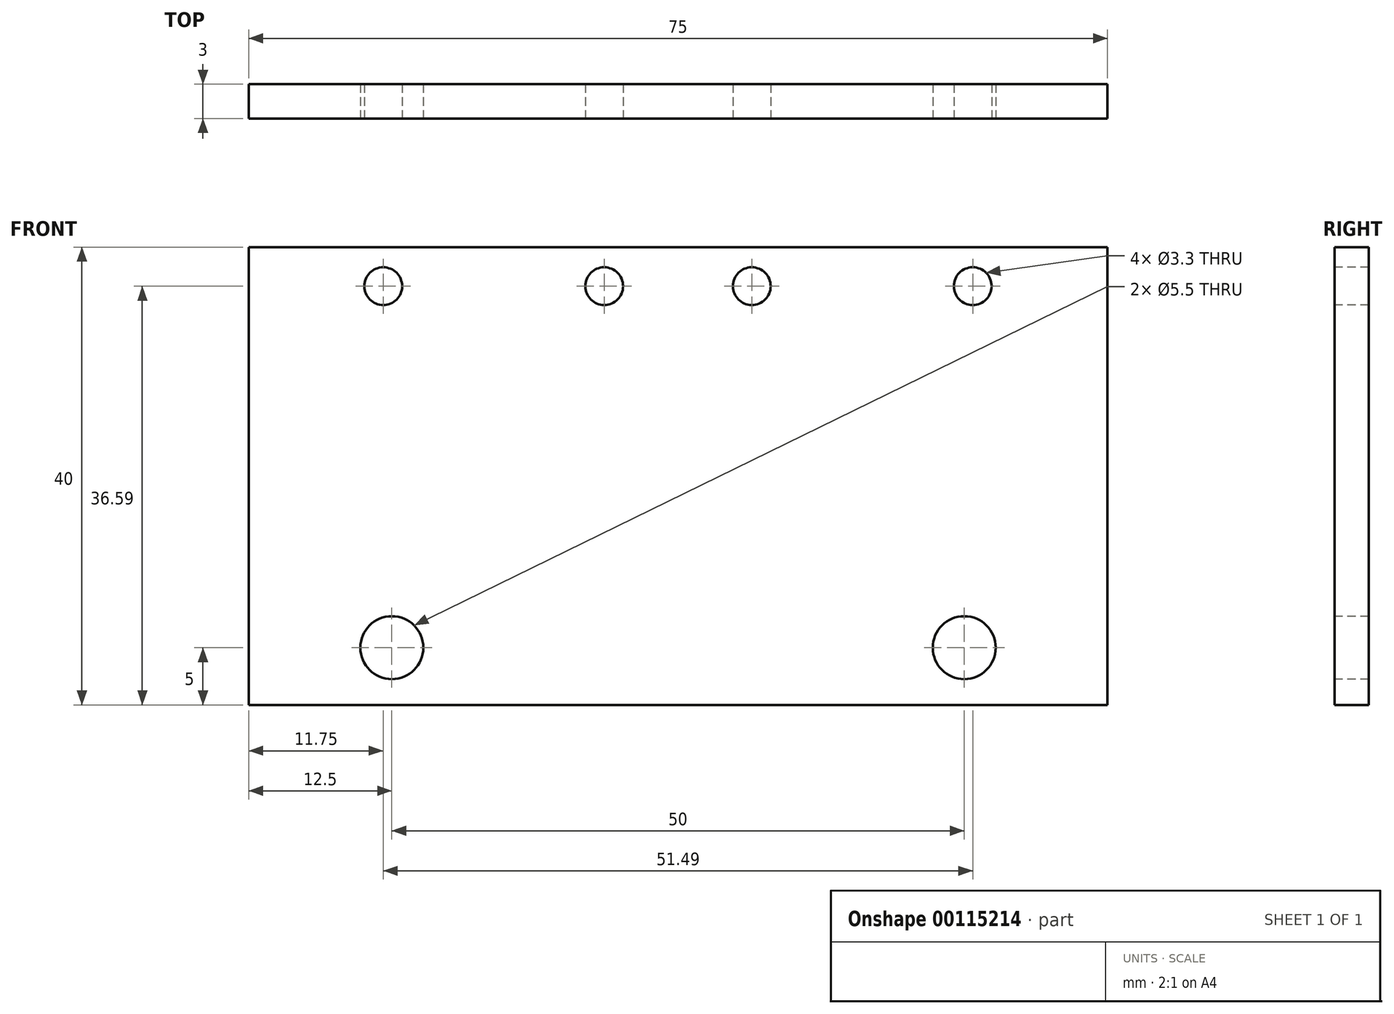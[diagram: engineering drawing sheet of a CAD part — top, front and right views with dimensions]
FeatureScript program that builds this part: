
annotation { "Feature Type Name" : "Feature", "Feature Type Description" : "" }
export const myFeature = defineFeature(function(context is Context, id is Id, definition is map)
    precondition{}
    {
        {
            var Q0;
            Q0=qCreatedBy(makeId("Front.planeOp"),FACE);
            var sketch = newSketch(context, id + "F0", { "sketchPlane" : qUnion([Q0])});
            skLineSegment(sketch, "E0.bottom", {"start": v(0, 0) * mm, "end": v(75, 0) * mm});
            skLineSegment(sketch, "E0.top", {"start": v(0, 40) * mm, "end": v(75, 40) * mm});
            skLineSegment(sketch, "E0.left", {"start": v(0, 0) * mm, "end": v(0, 40) * mm});
            skLineSegment(sketch, "E0.right", {"start": v(75, 0) * mm, "end": v(75, 40) * mm});
            skSolve(sketch);
        }
        {
            var Q0;
            Q0 = qSketchRegion(id + "F0", true);
            extrude(context, id + "F1", {"entities" : qUnion([Q0]), "oppositeDirection" : true, "depth" : 3 * mm});
        }
        {
            var Q0;
            Q0=makeQuery(id+"F1.opExtrude","CAP_FACE",FACE,{"disambiguationData":[OSD([sQuery(id+"F0.wireOp",EDGE,"E0.bottom"),sQuery(id+"F0.wireOp",EDGE,"E0.top"),sQuery(id+"F0.wireOp",EDGE,"E0.left"),sQuery(id+"F0.wireOp",EDGE,"E0.right")])],"isStart":true});
            var sketch = newSketch(context, id + "F2", { "sketchPlane" : qUnion([Q0])});
            skPoint(sketch, "E1", {"position": v(12.5, 5) * mm});
            skPoint(sketch, "E2", {"position": v(62.5, 5) * mm});
            skPoint(sketch, "E3", {"position": v(11.75, 36.6) * mm});
            skPoint(sketch, "E4", {"position": v(31.05, 36.6) * mm});
            skPoint(sketch, "E5", {"position": v(43.94, 36.6) * mm});
            skPoint(sketch, "E6", {"position": v(63.24, 36.6) * mm});
            skSolve(sketch);
        }
        {
            var Q0;
            Q0=sQuery(id+"F2.wireOp",VERTEX,"E1");
            var Q1;
            Q1=sQuery(id+"F2.wireOp",VERTEX,"E2");
            var Q2;
            Q2=makeQuery(id+"F1.opExtrude","SWEPT_BODY",BODY,{"disambiguationData":[OSD([sQuery(id+"F0.wireOp",EDGE,"E0.bottom"),sQuery(id+"F0.wireOp",EDGE,"E0.top"),sQuery(id+"F0.wireOp",EDGE,"E0.left"),sQuery(id+"F0.wireOp",EDGE,"E0.right")])]});
            hole(context, id + "F3", {"style" : HoleStyle.SIMPLE, "endStyle" : HoleEndStyle.THROUGH, "holeDiameter" : 5.5 * mm, "locations" : qUnion([Q0, Q1]), "scope" : qUnion([Q2]), "isTappedThrough" : true});
        }
        {
            var Q0;
            Q0=sQuery(id+"F2.wireOp",VERTEX,"E3");
            var Q1;
            Q1=sQuery(id+"F2.wireOp",VERTEX,"E4");
            var Q2;
            Q2=sQuery(id+"F2.wireOp",VERTEX,"E5");
            var Q3;
            Q3=sQuery(id+"F2.wireOp",VERTEX,"E6");
            var Q4;
            Q4=makeQuery(id+"F1.opExtrude","SWEPT_BODY",BODY,{"disambiguationData":[OSD([sQuery(id+"F0.wireOp",EDGE,"E0.bottom"),sQuery(id+"F0.wireOp",EDGE,"E0.top"),sQuery(id+"F0.wireOp",EDGE,"E0.left"),sQuery(id+"F0.wireOp",EDGE,"E0.right")])]});
            hole(context, id + "F4", {"style" : HoleStyle.SIMPLE, "endStyle" : HoleEndStyle.THROUGH, "holeDiameter" : 3.3 * mm, "locations" : qUnion([Q0, Q1, Q2, Q3]), "scope" : qUnion([Q4]), "isTappedThrough" : true});
        }
    });
